# Revit family: Hager-VECTOR-Surface_mounted-IP65-With_Cover-With_DIN-Hosted-BE-en
name_source: partatom
category: Electrical Equipment
units: mm (PartAtom-declared; Revit-internal decimal feet)

## family parameters
Cut with Voids When Loaded = No
Host = Face
Maintain Annotation Orientation = Yes
Panel Configuration = Two Columns, Circuits Across
Part Type = Panelboard
Room Calculation Point = No
Round Connector Dimension = Use Diameter
Shared = No

## types (26) — shared parameters
BC_MODEL_ID = 1546932
BC_OBJECT_ID = 513414
BC_OBJECT_VERSION = #3
Code hager = ADD-EC000214_EU
EF000003 - Mounting method = Surface mounted
EF000007 - Colour = Grey
EF000024 - UV resistant = No
EF000116 - RAL-number = 7035
EF000118 - With mounting plate = No
EF001062 - EMC-version = No
EF001088 - Extension possible = Yes
EF001134 - DIN-rail = Yes
EF004462 - Type of closure = Other
EF005474 - Degree of protection (IP) = IP65
EF006244 - Transparent cover/door = Yes
EF006306 - With lock = No
EF015941 - Signal passing door = Yes
ETIM class code = EC000214
ETIM class name = Small distribution board
HG000001-Number of columns = 1
HG000002-With door or cover = Yes
HG000003-Range = VECTOR
HG000005-Thickness = 2 mm  [stored 0.00656168 ft]
HG000006-Flush mounted = No
HG000009-Double swing door = No
HG000010-Asymmetric doors = No
HG000011-Empty rows from bottom = No
HG000012-Door swing angle = 90.00°
HG000013-Door on the left = No
HG000014-Door on the right = Yes
HG000015-Clearance visibility = Yes
HG000016-Door 3D visibility = Yes
HG000017-Distance between poles = 18 mm  [stored 0.0590551 ft]
HG000060-RAL-number = 7035
HG000099-Onfly Template ID = 507532
Manufacturer = Hager
Name = VECTOR-Surface_mounted-IP65-With_Cover-With_DIN-BE
Name BIM&CO = Electricity
Name hager = ADD_Enclosures_EC000214
Uniformat = Low Tension Service & Dist.
Uniformat code = D501001
zero-valued in all types: Default Elevation, EF000218 - Built-in depth, EF000332 - Built-in height, EF000846 - Built-in width, EF001131 - Inner depth, HG000007-Number of empty columns, HG000008-Number of empty rows

## per-type parameters (varying)
| type | BC_VARIANT_ID | EF000008 - Width | EF000040 - Height | EF000049 - Depth | EF000266 - Number of rows | EF002950 - Width in number of modular spacings | EF009212 - Cover model | EF015776 - Earthing terminal block | EF015777 - Neutral terminal block | HG000004-Manufacturer reference | HGEF000266-Number of rows | HGEF002950-Width in number of modular spacings |
| VECTOR-Surface_mounted_W110_H175_D93_3_Modular_Spacing-VE103D | 1173569 | 110 mm  [stored 0.360892 ft] | 175 mm  [stored 0.574147 ft] | 93 mm  [stored 0.305118 ft] | 1 | 3 | Closed | Yes | No | VE103D | 1 | 3 |
| VECTOR-Surface_mounted_W111_H175_D93_3_Modular_Spacing-VE103M | 1173573 | 111 mm | 175 mm  [stored 0.574147 ft] | 93 mm  [stored 0.305118 ft] | 1 | 3 | Closed | No | No | VE103M | 1 | 3 |
| VECTOR-Surface_mounted_W111_H175_D93_3_Modular_Spacing-VE103PN | 1173575 | 111 mm | 175 mm  [stored 0.574147 ft] | 93 mm  [stored 0.305118 ft] | 1 | 3 | With notch | No | No | VE103PN | 1 | 3 |
| VECTOR-Surface_mounted_W164_H190_D113_6_Modular_Spacing-VE106D | 1173576 | 164 mm  [stored 0.538058 ft] | 190 mm | 113 mm  [stored 0.370735 ft] | 1 | 6 | Closed | Yes | No | VE106D | 1 | 6 |
| VECTOR-Surface_mounted_W165_H190_D113_6_Modular_Spacing-VE106M | 1173577 | 165 mm | 190 mm | 113 mm  [stored 0.370735 ft] | 1 | 6 | Closed | Yes | No | VE106M | 1 | 6 |
| VECTOR-Surface_mounted_W165_H190_D113_6_Modular_Spacing-VE106PN | 1173579 | 165 mm | 190 mm | 113 mm  [stored 0.370735 ft] | 1 | 6 | Closed | No | No | VE106PN | 1 | 6 |
| VECTOR-Surface_mounted_W236_H210_D114_10_Modular_Spacing-VE110D | 1173580 | 236 mm | 210 mm  [stored 0.688976 ft] | 114 mm  [stored 0.374016 ft] | 1 | 10 | Closed | Yes | No | VE110D | 1 | 10 |
| VECTOR-Surface_mounted_W237_H210_D114_10_Modular_Spacing-VE110M | 1173581 | 237 mm  [stored 0.777559 ft] | 210 mm  [stored 0.688976 ft] | 114 mm  [stored 0.374016 ft] | 1 | 10 | Closed | Yes | No | VE110M | 1 | 10 |
| VECTOR-Surface_mounted_W237_H210_D114_10_Modular_Spacing-VE110PN | 1173584 | 237 mm  [stored 0.777559 ft] | 210 mm  [stored 0.688976 ft] | 114 mm  [stored 0.374016 ft] | 1 | 10 | Closed | No | No | VE110PN | 1 | 10 |
| VECTOR-Surface_mounted_W310_H302_D151_12_Modular_Spacing-VE112DN | 1173586 | 310 mm  [stored 1.01706 ft] | 302 mm  [stored 0.990814 ft] | 151 mm  [stored 0.495407 ft] | 1 | 12 | Closed | Yes | Yes | VE112DN | 1 | 12 |
| VECTOR-Surface_mounted_W310_H302_D151_12_Modular_Spacing-VE112M | 1173588 | 310 mm  [stored 1.01706 ft] | 302 mm  [stored 0.990814 ft] | 151 mm  [stored 0.495407 ft] | 1 | 12 | Closed | Yes | No | VE112M | 1 | 12 |
| VECTOR-Surface_mounted_W310_H302_D151_12_Modular_Spacing-VE112PN | 1173591 | 310 mm  [stored 1.01706 ft] | 302 mm  [stored 0.990814 ft] | 151 mm  [stored 0.495407 ft] | 1 | 12 | Closed | No | No | VE112PN | 1 | 12 |
| VECTOR-Surface_mounted_W418_H302_D151_18_Modular_Spacing-VE118M | 1173593 | 418 mm  [stored 1.37139 ft] | 302 mm  [stored 0.990814 ft] | 151 mm  [stored 0.495407 ft] | 1 | 18 | Closed | Yes | No | VE118M | 1 | 18 |
| VECTOR-Surface_mounted_W418_H302_D151_18_Modular_Spacing-VE118PN | 1173595 | 418 mm  [stored 1.37139 ft] | 302 mm  [stored 0.990814 ft] | 151 mm  [stored 0.495407 ft] | 1 | 18 | Closed | No | No | VE118PN | 1 | 18 |
| VECTOR-Surface_mounted_W310_H427_D151_12_Modular_Spacing-VE212DN | 1173597 | 310 mm  [stored 1.01706 ft] | 427 mm  [stored 1.40092 ft] | 151 mm  [stored 0.495407 ft] | 2 | 12 | Closed | Yes | Yes | VE212DN | 2 | 12 |
| VECTOR-Surface_mounted_W310_H427_D151_12_Modular_Spacing-VE212M | 1173600 | 310 mm  [stored 1.01706 ft] | 427 mm  [stored 1.40092 ft] | 151 mm  [stored 0.495407 ft] | 2 | 12 | Closed | Yes | No | VE212M | 2 | 12 |
| VECTOR-Surface_mounted_W310_H427_D151_12_Modular_Spacing-VE212PN | 1173602 | 310 mm  [stored 1.01706 ft] | 427 mm  [stored 1.40092 ft] | 151 mm  [stored 0.495407 ft] | 2 | 12 | Closed | No | No | VE212PN | 2 | 12 |
| VECTOR-Surface_mounted_W418_H452_D151_18_Modular_Spacing-VE218M | 1173604 | 418 mm  [stored 1.37139 ft] | 452 mm  [stored 1.48294 ft] | 151 mm  [stored 0.495407 ft] | 2 | 18 | Closed | Yes | No | VE218M | 2 | 18 |
| VECTOR-Surface_mounted_W418_H452_D151_18_Modular_Spacing-VE218PN | 1173607 | 418 mm  [stored 1.37139 ft] | 452 mm  [stored 1.48294 ft] | 151 mm  [stored 0.495407 ft] | 2 | 18 | Closed | No | No | VE218PN | 2 | 18 |
| VECTOR-Surface_mounted_W310_H552_D151_12_Modular_Spacing-VE312DN | 1173610 | 310 mm  [stored 1.01706 ft] | 552 mm  [stored 1.81102 ft] | 151 mm  [stored 0.495407 ft] | 3 | 12 | Closed | Yes | Yes | VE312DN | 3 | 12 |
| VECTOR-Surface_mounted_W310_H552_D151_12_Modular_Spacing-VE312M | 1173612 | 310 mm  [stored 1.01706 ft] | 552 mm  [stored 1.81102 ft] | 151 mm  [stored 0.495407 ft] | 3 | 12 | Closed | Yes | No | VE312M | 3 | 12 |
| VECTOR-Surface_mounted_W310_H552_D151_12_Modular_Spacing-VE312PN | 1173615 | 310 mm  [stored 1.01706 ft] | 552 mm  [stored 1.81102 ft] | 151 mm  [stored 0.495407 ft] | 3 | 12 | Closed | No | No | VE312PN | 3 | 12 |
| VECTOR-Surface_mounted_W418_H602_D151_18_Modular_Spacing-VE318M | 1173617 | 418 mm  [stored 1.37139 ft] | 602 mm  [stored 1.97507 ft] | 151 mm  [stored 0.495407 ft] | 3 | 18 | Closed | Yes | No | VE318M | 3 | 18 |
| VECTOR-Surface_mounted_W418_H602_D151_18_Modular_Spacing-VE318PN | 1173620 | 418 mm  [stored 1.37139 ft] | 602 mm  [stored 1.97507 ft] | 151 mm  [stored 0.495407 ft] | 3 | 18 | Closed | No | No | VE318PN | 3 | 18 |
| VECTOR-Surface_mounted_W310_H677_D151_12_Modular_Spacing-VE412M | 1173622 | 310 mm  [stored 1.01706 ft] | 677 mm  [stored 2.22113 ft] | 151 mm  [stored 0.495407 ft] | 4 | 12 | Closed | No | No | VE412M | 4 | 12 |
| VECTOR-Surface_mounted_W310_H677_D151_12_Modular_Spacing-VE412PN | 1173625 | 310 mm  [stored 1.01706 ft] | 677 mm  [stored 2.22113 ft] | 151 mm  [stored 0.495407 ft] | 4 | 12 | Closed | No | No | VE412PN | 4 | 12 |

note: column(s) folded — value = type name in every type: Reference

note: [stored X ft] marks values corroborated as IEEE doubles in the binary element streams (Revit-internal decimal feet)

## geometry (parser evidence)
native form markers: Sweep x14
no freeform markers — native parametric forms only
